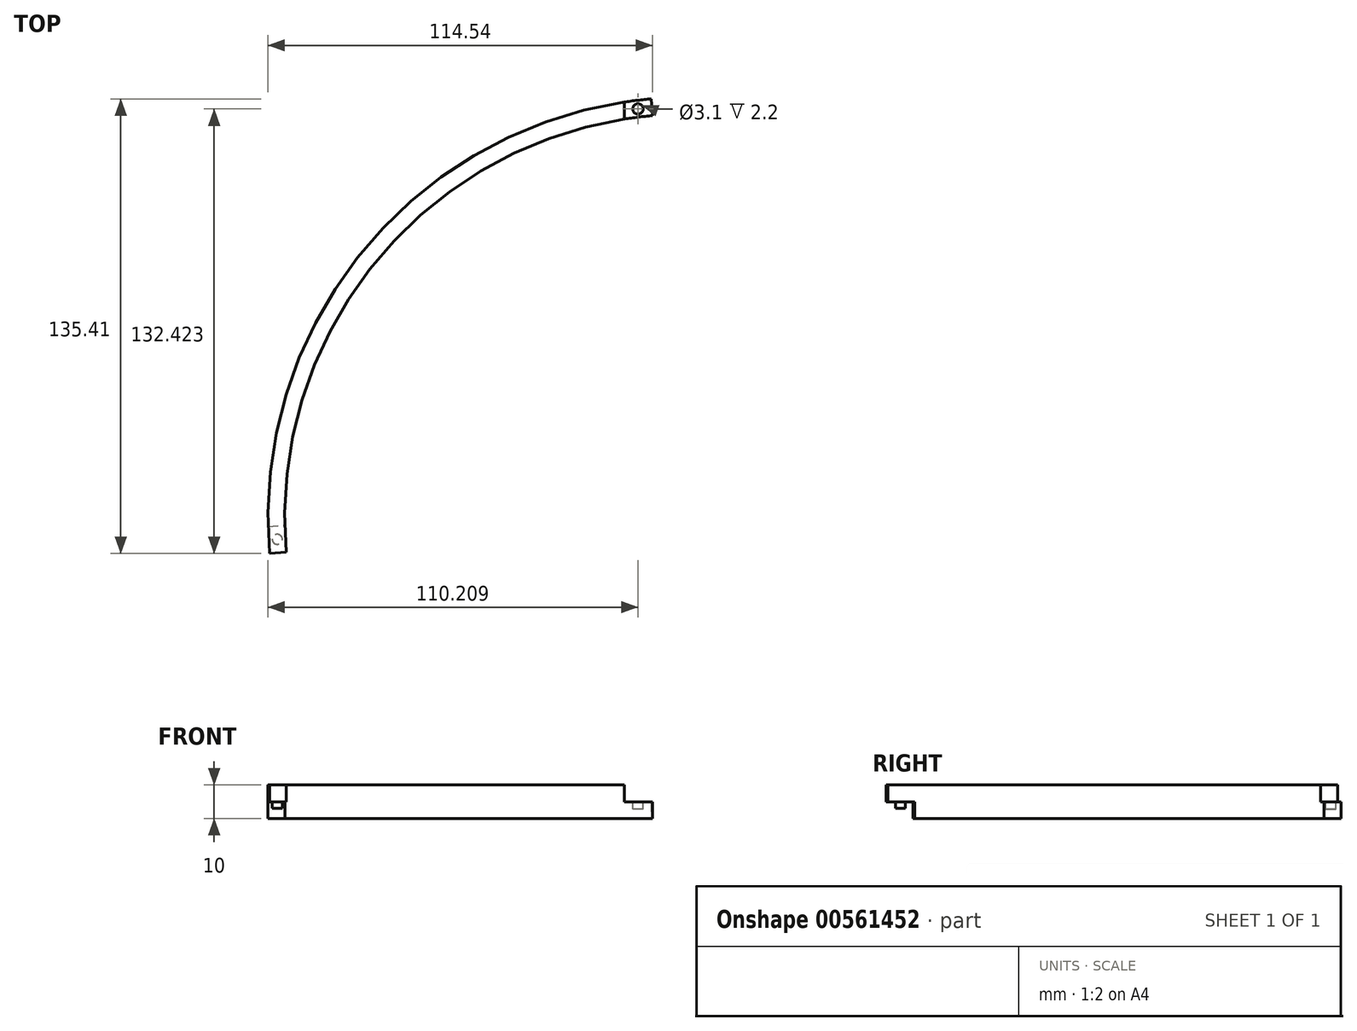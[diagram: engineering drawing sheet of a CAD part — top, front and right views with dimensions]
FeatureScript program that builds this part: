
annotation { "Feature Type Name" : "Feature", "Feature Type Description" : "" }
export const myFeature = defineFeature(function(context is Context, id is Id, definition is map)
    precondition{}
    {
        {
            var Q0;
            Q0=qCreatedBy(makeId("Top.planeOp"),FACE);
            var sketch = newSketch(context, id + "F0", { "sketchPlane" : qUnion([Q0])});
            skLineSegment(sketch, "E0", {"start": v(0, 166.79) * mm, "end": v(0, -153.79) * mm, "construction": true});
            skLineSegment(sketch, "E1", {"start": v(-142.95, 0) * mm, "end": v(164.94, 0) * mm, "construction": true});
            skLineSegment(sketch, "E2", {"start": v(-127.31, -11.14) * mm, "end": v(193.86, 16.96) * mm, "construction": true});
            skArc(sketch, "E3", {"start": v(-10.46, 119.54) * mm, "mid": v(-91.93, 77.13) * mm, "end": v(-119.54, -10.46) * mm});
            skArc(sketch, "E4", {"start": v(-10.9, 124.52) * mm, "mid": v(-95.76, 80.35) * mm, "end": v(-124.52, -10.9) * mm});
            skLineSegment(sketch, "E5", {"start": v(-10.9, 124.52) * mm, "end": v(-10.9, 124.52) * mm});
            skLineSegment(sketch, "E6", {"start": v(-124.52, -10.9) * mm, "end": v(-119.54, -10.46) * mm});
            skLineSegment(sketch, "E7", {"start": v(8.29, -94.72) * mm, "end": v(-14.97, 171.06) * mm, "construction": true});
            skLineSegment(sketch, "E8", {"start": v(-10.46, 119.54) * mm, "end": v(-10.9, 124.52) * mm});
            skSolve(sketch);
        }
        {
            var Q0;
            Q0=makeQuery(id+"F0.imprint","IMPRINT",FACE,{"disambiguationData":[TD([[makeQuery(id+"F0.imprint","IMPRINT",EDGE,{"derivedFrom":sQuery(id+"F0.wireOp",EDGE,"E3")}),-1.0]])]});
            extrude(context, id + "F1", {"entities" : qUnion([Q0]), "depth" : 10 * mm, "offsetDistance" : 25 * mm});
        }
        {
            var Q0;
            Q0=makeQuery(id+"F1.opExtrude","CAP_FACE",FACE,{"disambiguationData":[OSD([sQuery(id+"F0.wireOp",EDGE,"E3"),sQuery(id+"F0.wireOp",EDGE,"E4"),sQuery(id+"F0.wireOp",EDGE,"E5"),sQuery(id+"F0.wireOp",EDGE,"E6")])],"isStart":true});
            var sketch = newSketch(context, id + "F2", { "sketchPlane" : qUnion([Q0])});
            skArc(sketch, "E9", {"start": v(-119.54, 10.46) * mm, "mid": v(-119.83, 6.46) * mm, "end": v(-119.97, 2.46) * mm});
            skArc(sketch, "E10", {"start": v(-124.52, 10.9) * mm, "mid": v(-124.8, 6.9) * mm, "end": v(-124.97, 2.9) * mm});
            skLineSegment(sketch, "E11", {"start": v(-124.52, 10.9) * mm, "end": v(-119.54, 10.46) * mm});
            skLineSegment(sketch, "E12", {"start": v(-124.97, 2.9) * mm, "end": v(-119.97, 2.46) * mm});
            skSolve(sketch);
        }
        {
            var Q0;
            Q0 = qSketchRegion(id + "F2", true);
            extrude(context, id + "F3", {"entities" : qUnion([Q0]), "operationType" : NewBodyOperationType.REMOVE, "oppositeDirection" : true, "depth" : 5 * mm, "offsetDistance" : 25 * mm});
        }
        {
            var Q0;
            Q0=makeQuery(id+"F1.opExtrude","CAP_FACE",FACE,{"disambiguationData":[OSD([sQuery(id+"F0.wireOp",EDGE,"E3"),sQuery(id+"F0.wireOp",EDGE,"E4"),sQuery(id+"F0.wireOp",EDGE,"E5"),sQuery(id+"F0.wireOp",EDGE,"E6")])],"isStart":false});
            var sketch = newSketch(context, id + "F4", { "sketchPlane" : qUnion([Q0])});
            skArc(sketch, "E13", {"start": v(-10.46, 119.54) * mm, "mid": v(-14.69, 119.1) * mm, "end": v(-18.9, 118.5) * mm});
            skArc(sketch, "E14", {"start": v(-10.9, 124.52) * mm, "mid": v(-14.9, 124.1) * mm, "end": v(-18.9, 123.56) * mm});
            skLineSegment(sketch, "E15", {"start": v(-18.9, 123.56) * mm, "end": v(-18.9, 118.5) * mm});
            skLineSegment(sketch, "E16", {"start": v(-10.9, 124.52) * mm, "end": v(-10.46, 119.54) * mm});
            skSolve(sketch);
        }
        {
            var Q0;
            Q0 = qSketchRegion(id + "F4", true);
            extrude(context, id + "F5", {"entities" : qUnion([Q0]), "operationType" : NewBodyOperationType.REMOVE, "oppositeDirection" : true, "depth" : 5 * mm, "offsetDistance" : 25 * mm});
        }
        {
            var Q0;
            Q0=makeQuery(id+"F3.boolean.opBoolean","COPY",FACE,{"derivedFrom":makeQuery(id+"F3.opExtrude","CAP_FACE",FACE,{"disambiguationData":[OSD([sQuery(id+"F2.wireOp",EDGE,"E9"),sQuery(id+"F2.wireOp",EDGE,"E10"),sQuery(id+"F2.wireOp",EDGE,"E11"),sQuery(id+"F2.wireOp",EDGE,"E12")])],"isStart":false})});
            var sketch = newSketch(context, id + "F6", { "sketchPlane" : qUnion([Q0])});
            skLineSegment(sketch, "E17", {"start": v(-122.03, 10.68) * mm, "end": v(-122.47, 1.28) * mm, "construction": true});
            skPoint(sketch, "E17.endSnap0", {"position": v(-122.47, 2.68) * mm});
            skLineSegment(sketch, "E18", {"start": v(-124.8, 6.9) * mm, "end": v(-119.35, 6.46) * mm, "construction": true});
            skPoint(sketch, "E18.endSnap0", {"position": v(-119.83, 6.46) * mm});
            skCircle(sketch, "E19", {"center": v(-122.22, 6.7) * mm, "radius": 1.5 * mm});
            skSolve(sketch);
        }
        {
            var Q0;
            Q0=makeQuery(id+"F6.imprint","IMPRINT",FACE,{"disambiguationData":[TD([[makeQuery(id+"F6.imprint","IMPRINT",EDGE,{"derivedFrom":sQuery(id+"F6.wireOp",EDGE,"E19")}),1.0]])]});
            extrude(context, id + "F7", {"entities" : qUnion([Q0]), "operationType" : NewBodyOperationType.ADD, "depth" : 2 * mm, "offsetDistance" : 25 * mm});
        }
        {
            var Q0;
            Q0=makeQuery(id+"F5.boolean.opBoolean","COPY",FACE,{"derivedFrom":makeQuery(id+"F5.opExtrude","CAP_FACE",FACE,{"disambiguationData":[OSD([sQuery(id+"F4.wireOp",EDGE,"E13"),sQuery(id+"F4.wireOp",EDGE,"E14"),sQuery(id+"F4.wireOp",EDGE,"E15"),sQuery(id+"F4.wireOp",EDGE,"E16")])],"isStart":false})});
            var sketch = newSketch(context, id + "F8", { "sketchPlane" : qUnion([Q0])});
            skCircle(sketch, "E20", {"center": v(-14.8, 121.53) * mm, "radius": 1.55 * mm});
            skLineSegment(sketch, "E21", {"start": v(-10.68, 122.03) * mm, "end": v(-18.9, 121.03) * mm, "construction": true});
            skLineSegment(sketch, "E22", {"start": v(-14.9, 124.1) * mm, "end": v(-14.69, 119.1) * mm, "construction": true});
            skSolve(sketch);
        }
        {
            var Q0;
            Q0=makeQuery(id+"F8.imprint","IMPRINT",FACE,{"disambiguationData":[TD([[makeQuery(id+"F8.imprint","IMPRINT",EDGE,{"derivedFrom":sQuery(id+"F8.wireOp",EDGE,"E20")}),1.0]])]});
            extrude(context, id + "F9", {"entities" : qUnion([Q0]), "operationType" : NewBodyOperationType.REMOVE, "oppositeDirection" : true, "depth" : 2.2 * mm, "offsetDistance" : 25 * mm});
        }
    });
